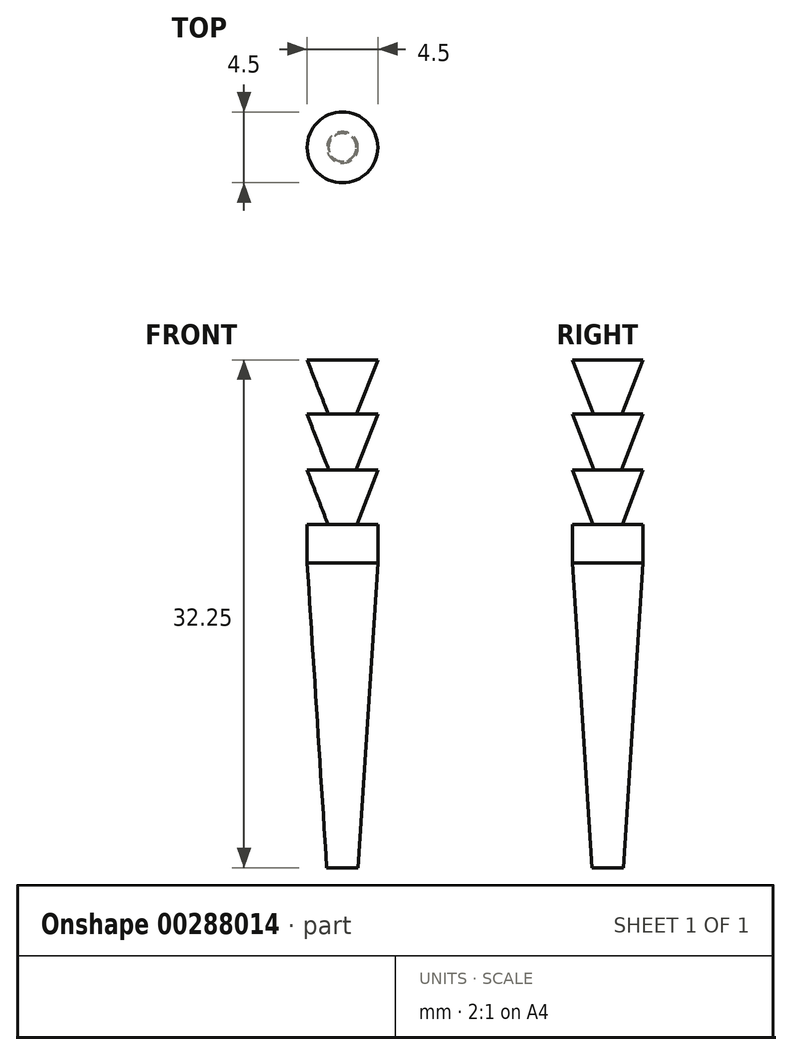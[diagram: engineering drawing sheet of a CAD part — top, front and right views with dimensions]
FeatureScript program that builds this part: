
annotation { "Feature Type Name" : "Feature", "Feature Type Description" : "" }
export const myFeature = defineFeature(function(context is Context, id is Id, definition is map)
    precondition{}
    {
        {
            var Q0;
            Q0=qCreatedBy(makeId("Front.planeOp"),FACE);
            var sketch = newSketch(context, id + "F0", { "sketchPlane" : qUnion([Q0])});
            skLineSegment(sketch, "E0", {"start": v(0, 0) * mm, "end": v(0, 30) * mm});
            skCircle(sketch, "E1", {"center": v(0, 30) * mm, "radius": 2.25 * mm, "construction": true});
            skCircle(sketch, "E2.1.0.0", {"center": v(0, 26.5) * mm, "radius": 2.25 * mm, "construction": true});
            skCircle(sketch, "E2.2.0.0", {"center": v(0, 23) * mm, "radius": 2.25 * mm, "construction": true});
            skCircle(sketch, "E2.3.0.0", {"center": v(0, 19.5) * mm, "radius": 2.25 * mm, "construction": true});
            skLineSegment(sketch, "E2.direction1", {"start": v(0, 30) * mm, "end": v(0, 26.5) * mm, "construction": true});
            skLineSegment(sketch, "E3", {"start": v(0, 0) * mm, "end": v(1, 0) * mm});
            skLineSegment(sketch, "E4", {"start": v(1, 0) * mm, "end": v(2.25, 19.36) * mm});
            skLineSegment(sketch, "E5", {"start": v(0, 30) * mm, "end": v(0, 32.25) * mm});
            skLineSegment(sketch, "E6", {"start": v(0, 32.25) * mm, "end": v(2.25, 29.86) * mm, "construction": true});
            skLineSegment(sketch, "E7", {"start": v(2.25, 29.86) * mm, "end": v(0, 27.75) * mm, "construction": true});
            skLineSegment(sketch, "E8", {"start": v(0, 28.75) * mm, "end": v(2.25, 26.64) * mm, "construction": true});
            skLineSegment(sketch, "E9", {"start": v(2.25, 26.64) * mm, "end": v(0, 24.25) * mm, "construction": true});
            skLineSegment(sketch, "E10", {"start": v(0, 25.25) * mm, "end": v(2.25, 22.86) * mm, "construction": true});
            skLineSegment(sketch, "E11", {"start": v(2.25, 22.86) * mm, "end": v(0, 20.75) * mm, "construction": true});
            skLineSegment(sketch, "E12", {"start": v(0, 21.75) * mm, "end": v(2.25, 19.36) * mm});
            skPoint(sketch, "E13", {"position": v(-2.25, 30) * mm});
            skLineSegment(sketch, "E14", {"start": v(2.25, 32.25) * mm, "end": v(-2.25, 32.25) * mm});
            skLineSegment(sketch, "E15", {"start": v(-2.25, 32.25) * mm, "end": v(0, 26.5) * mm});
            skLineSegment(sketch, "E16", {"start": v(2.25, 32.25) * mm, "end": v(0, 26.5) * mm});
            skLineSegment(sketch, "E17", {"start": v(-2.25, 28.75) * mm, "end": v(2.25, 28.8) * mm});
            skPoint(sketch, "E17.endSnap0", {"position": v(1.12, 28.8) * mm});
            skLineSegment(sketch, "E18", {"start": v(2.25, 28.8) * mm, "end": v(0, 23) * mm});
            skLineSegment(sketch, "E19", {"start": v(-2.25, 28.75) * mm, "end": v(0, 23) * mm});
            skLineSegment(sketch, "E20", {"start": v(-2.25, 25.25) * mm, "end": v(2.25, 25.25) * mm});
            skLineSegment(sketch, "E21", {"start": v(2.25, 25.25) * mm, "end": v(0, 19.4) * mm});
            skLineSegment(sketch, "E22", {"start": v(0, 19.4) * mm, "end": v(-2.25, 25.25) * mm});
            skLineSegment(sketch, "E23", {"start": v(2.25, 21.8) * mm, "end": v(2.25, 19.36) * mm});
            skPoint(sketch, "E23.startSnap0", {"position": v(1.12, 21.8) * mm});
            skLineSegment(sketch, "E24", {"start": v(0, 21.75) * mm, "end": v(2.25, 21.8) * mm});
            skSolve(sketch);
        }
        {
            var Q0;
            {var subQ0=sQuery(id+"F0.wireOp",EDGE,"E24");var subQ3=sQuery(id+"F0.wireOp",EDGE,"E21");var subQ5=makeQuery(id+"F0.imprint","INTERSECT",VERTEX,{"derivedFrom":[subQ3,subQ0]});Q0=makeQuery(id+"F0.imprint","IMPRINT",FACE,{"disambiguationData":[TD([[makeQuery(id+"F0.imprint","IMPRINT",EDGE,{"disambiguationData":[TD([[subQ5,-1.0]])],"derivedFrom":subQ3}),-1.0]])]});}
            var Q1;
            {var subQ0=sQuery(id+"F0.wireOp",EDGE,"E23");Q1=makeQuery(id+"F0.imprint","IMPRINT",FACE,{"disambiguationData":[TD([[makeQuery(id+"F0.imprint","IMPRINT",EDGE,{"derivedFrom":subQ0}),-1.0]])]});}
            var Q2;
            {var subQ0=sQuery(id+"F0.wireOp",EDGE,"E12");var subQ3=sQuery(id+"F0.wireOp",EDGE,"E21");var subQ5=makeQuery(id+"F0.imprint","INTERSECT",VERTEX,{"derivedFrom":[subQ0,subQ3]});Q2=makeQuery(id+"F0.imprint","IMPRINT",FACE,{"disambiguationData":[TD([[makeQuery(id+"F0.imprint","IMPRINT",EDGE,{"disambiguationData":[TD([[subQ5,1.0]])],"derivedFrom":subQ0}),-1.0]])]});}
            var Q3;
            {var subQ0=sQuery(id+"F0.wireOp",EDGE,"E21");var subQ1=sQuery(id+"F0.wireOp",EDGE,"E20");var subQ2=makeQuery(id+"F0.imprint","INTERSECT",VERTEX,{"derivedFrom":[subQ1,subQ0]});Q3=makeQuery(id+"F0.imprint","IMPRINT",FACE,{"disambiguationData":[TD([[makeQuery(id+"F0.imprint","IMPRINT",EDGE,{"disambiguationData":[TD([[subQ2,1.0]])],"derivedFrom":subQ1}),-1.0]])]});}
            var Q4;
            {var subQ0=sQuery(id+"F0.wireOp",EDGE,"E18");var subQ3=sQuery(id+"F0.wireOp",EDGE,"E20");var subQ5=makeQuery(id+"F0.imprint","INTERSECT",VERTEX,{"derivedFrom":[subQ0,subQ3]});Q4=makeQuery(id+"F0.imprint","IMPRINT",FACE,{"disambiguationData":[TD([[makeQuery(id+"F0.imprint","IMPRINT",EDGE,{"disambiguationData":[TD([[subQ5,1.0]])],"derivedFrom":subQ3}),-1.0]])]});}
            var Q5;
            {var subQ0=sQuery(id+"F0.wireOp",EDGE,"E18");var subQ1=sQuery(id+"F0.wireOp",EDGE,"E17");var subQ2=makeQuery(id+"F0.imprint","INTERSECT",VERTEX,{"derivedFrom":[subQ1,subQ0]});Q5=makeQuery(id+"F0.imprint","IMPRINT",FACE,{"disambiguationData":[TD([[makeQuery(id+"F0.imprint","IMPRINT",EDGE,{"disambiguationData":[TD([[subQ2,1.0]])],"derivedFrom":subQ1}),-1.0]])]});}
            var Q6;
            {var subQ0=sQuery(id+"F0.wireOp",EDGE,"E16");var subQ3=sQuery(id+"F0.wireOp",EDGE,"E17");var subQ5=makeQuery(id+"F0.imprint","INTERSECT",VERTEX,{"derivedFrom":[subQ0,subQ3]});Q6=makeQuery(id+"F0.imprint","IMPRINT",FACE,{"disambiguationData":[TD([[makeQuery(id+"F0.imprint","IMPRINT",EDGE,{"disambiguationData":[TD([[subQ5,1.0]])],"derivedFrom":subQ3}),-1.0]])]});}
            var Q7;
            {var subQ1=sQuery(id+"F0.wireOp",EDGE,"E5");Q7=makeQuery(id+"F0.imprint","IMPRINT",FACE,{"disambiguationData":[TD([[makeQuery(id+"F0.imprint","IMPRINT",EDGE,{"derivedFrom":subQ1}),-1.0]])]});}
            var Q8;
            {var subQ4=sQuery(id+"F0.wireOp",EDGE,"E3");Q8=makeQuery(id+"F0.imprint","IMPRINT",FACE,{"disambiguationData":[TD([[makeQuery(id+"F0.imprint","IMPRINT",EDGE,{"derivedFrom":subQ4}),1.0]])]});}
            var Q9;
            Q9=sQuery(id+"F0.wireOp",EDGE,"E0");
            revolve(context, id + "F1", {"entities" : qUnion([Q0, Q1, Q2, Q3, Q4, Q5, Q6, Q7, Q8]), "axis" : qUnion([Q9]), "revolveType" : RevolveType.FULL});
        }
    });
